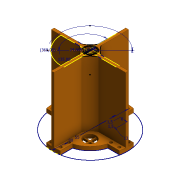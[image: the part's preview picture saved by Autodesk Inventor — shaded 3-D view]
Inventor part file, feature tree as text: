
AUTODESK INVENTOR PART (.ipt)
format: ipt  version: 2020.3 (Build 243373000, 373)  size: 316,416 bytes
history: native  units: mm
features: extrude x10, sketch x7, pattern_circular x3
ambient origin geometry x8: Origin, YZ Plane, XZ Plane, XY Plane, X Axis, Y Axis, Z Axis, Center Point
bodies: Solid1 (feature_tree)
feature tree (20):
  extrude  "Extrusion1"  Depth=4.0mm TaperAngle=0.0deg
  extrude  "Extrusion2"  Depth=3.0mm
  sketch  "Sketch5"  dims[d7=3.0mm d8=3.0mm]
  extrude  "Extrusion5"  Depth=3.0mm
  extrude  "Extrusion6"  Depth=70.0mm
  pattern_circular  "Circular Pattern1"  Count=4 Angle=360.0deg
  sketch  "Sketch8"  dims[d9=70.0mm d10=0.0mm d20=13.0mm]
  extrude  "Extrusion13"  Depth=1.5mm
  extrude  "Extrusion14"  Depth=1.5mm
  pattern_circular  "Circular Pattern3"  [2 undecoded]
  extrude  "Extrusion15"  Depth=3.0mm
  sketch  "Sketch10"  dims[d25=8.0mm]
  extrude  "Extrusion17"  Depth=3.0mm
  extrude  "Extrusion18"  Depth=1.5mm
  extrude  "Extrusion19"  Depth=24.665113mm
  pattern_circular  "Circular Pattern4"  Angle=45.0deg  [1 undecoded]
  sketch  "Sketch12"  dims[d28=4.0mm d29=0.0mm d33=40.0mm d34=360.0deg d58=1.5mm d59=1.5mm d84=15.0mm d85=13.0mm d86=11.0mm d87=1.5mm d88=24.665113mm d89=45.0deg d90=40.0mm d92=360.0deg d94=13.0mm d95=0.0mm d96=10.0mm d97=0.0mm d98=40.0mm d99=360.0deg d101=2.0mm d102=0.0mm d106=55.0mm d107=80.0mm d108=10.0mm d109=0.0mm d110=10.0mm d111=0.0mm d112=6.0mm d113=3.0mm d114=7.5mm d115=3.0mm d116=36.0mm d117=36.0mm d118=3.0mm d119=3.0mm d120=6.25mm d121=0.0mm d122=40.0mm d123=360.0deg d125=3.0mm d75=0.5mm d76=0.872665mm d77=0.5mm d78=0.872665mm]
  sketch  "Sketch1"  dims[d0=60.0mm d1=4.0mm d2=0.0mm]
  sketch  "Sketch2"  dims[d5=3.0mm d6=3.0mm]
  sketch  "Sketch11"  dims[d26=2.0mm d27=0.0mm]
note: 3 required parameter values undecoded (feature->parameter linkage not recoverable at this tier; creation-order binding heuristic only, values carry confidence <= 0.55)
